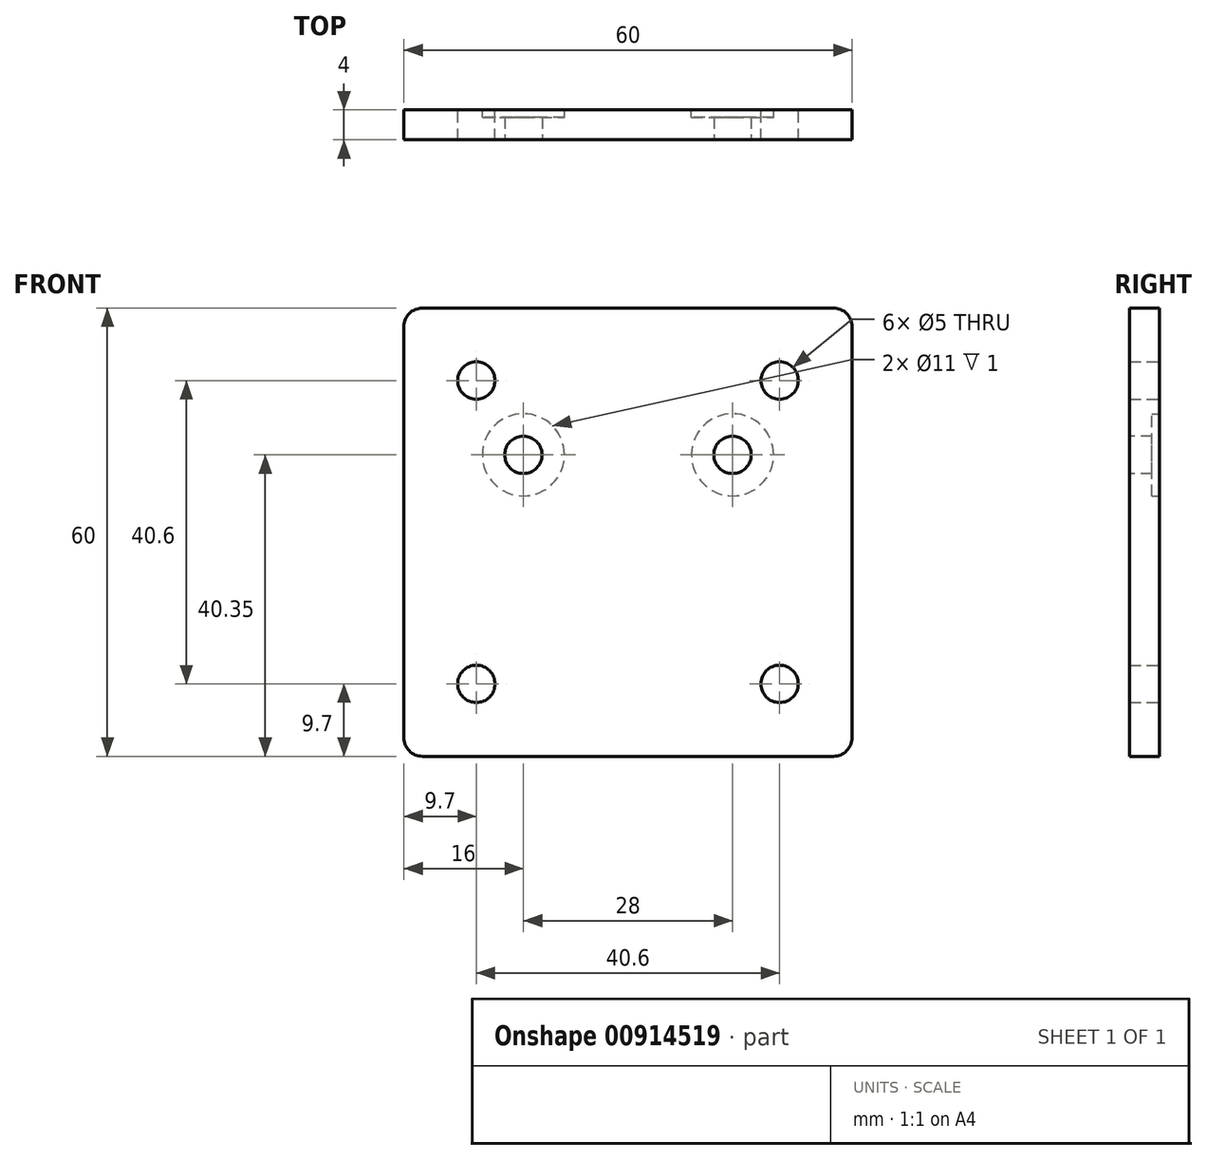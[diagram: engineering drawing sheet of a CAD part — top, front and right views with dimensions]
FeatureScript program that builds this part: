
annotation { "Feature Type Name" : "Feature", "Feature Type Description" : "" }
export const myFeature = defineFeature(function(context is Context, id is Id, definition is map)
    precondition{}
    {
        {
            var Q0;
            Q0=qCreatedBy(makeId("Front.planeOp"),FACE);
            var sketch = newSketch(context, id + "F0", { "sketchPlane" : qUnion([Q0])});
            skLineSegment(sketch, "E0.bottom", {"start": v(30, 30) * mm, "end": v(-30, 30) * mm});
            skLineSegment(sketch, "E0.top", {"start": v(30, -30) * mm, "end": v(-30, -30) * mm});
            skLineSegment(sketch, "E0.left", {"start": v(30, 30) * mm, "end": v(30, -30) * mm});
            skLineSegment(sketch, "E0.right", {"start": v(-30, 30) * mm, "end": v(-30, -30) * mm});
            skPoint(sketch, "E0.middle", {"position": v(0, 0) * mm});
            skLineSegment(sketch, "E1", {"start": v(20.3, 30) * mm, "end": v(20.3, -30) * mm, "construction": true});
            skLineSegment(sketch, "E2", {"start": v(30, 20.3) * mm, "end": v(-30, 20.3) * mm, "construction": true});
            skLineSegment(sketch, "E3.MirrorCS", {"start": v(-20.3, 30) * mm, "end": v(-20.3, -30) * mm, "construction": true});
            skLineSegment(sketch, "E4.MirrorCS", {"start": v(30, -20.3) * mm, "end": v(-30, -20.3) * mm, "construction": true});
            skPoint(sketch, "E5", {"position": v(-20.3, 20.3) * mm});
            skPoint(sketch, "E6", {"position": v(20.3, 20.3) * mm});
            skPoint(sketch, "E7", {"position": v(20.3, -20.3) * mm});
            skPoint(sketch, "E8", {"position": v(-20.3, -20.3) * mm});
            skSolve(sketch);
        }
        {
            var Q0;
            Q0=qSketchRegion(id+"F0",true);
            extrude(context, id + "F1", {"entities" : qUnion([Q0]), "depth" : 4 * mm, "offsetDistance" : 25 * mm});
        }
        {
            var Q0;
            Q0=sQuery(id+"F0.wireOp",VERTEX,"E8");
            var Q1;
            Q1=sQuery(id+"F0.wireOp",VERTEX,"E7");
            var Q2;
            Q2=sQuery(id+"F0.wireOp",VERTEX,"E6");
            var Q3;
            Q3=sQuery(id+"F0.wireOp",VERTEX,"E5");
            var Q4;
            Q4=makeQuery(id+"F1.opExtrude","SWEPT_BODY",BODY,{"disambiguationData":[OSD([sQuery(id+"F0.wireOp",EDGE,"E0.bottom"),sQuery(id+"F0.wireOp",EDGE,"E0.top"),sQuery(id+"F0.wireOp",EDGE,"E0.left"),sQuery(id+"F0.wireOp",EDGE,"E0.right")])]});
            hole(context, id + "F2", {"style" : HoleStyle.SIMPLE, "endStyle" : HoleEndStyle.THROUGH, "oppositeDirection" : true, "holeDiameter" : 5 * mm, "majorDiameter" : 5 * mm, "isTappedThrough" : true, "tappedDepth" : 12 * mm, "tapClearance" : 3, "locations" : qUnion([Q0, Q1, Q2, Q3]), "scope" : qUnion([Q4])});
        }
        {
            var Q0;
            Q0=makeQuery(id+"F1.opExtrude","CAP_FACE",FACE,{"disambiguationData":[OSD([sQuery(id+"F0.wireOp",EDGE,"E0.bottom"),sQuery(id+"F0.wireOp",EDGE,"E0.top"),sQuery(id+"F0.wireOp",EDGE,"E0.left"),sQuery(id+"F0.wireOp",EDGE,"E0.right")])],"isStart":false});
            var sketch = newSketch(context, id + "F3", { "sketchPlane" : qUnion([Q0])});
            skPoint(sketch, "E9", {"position": v(-14, 10.35) * mm});
            skLineSegment(sketch, "E10", {"start": v(-14, 10.35) * mm, "end": v(0, 10.35) * mm, "construction": true});
            skLineSegment(sketch, "E11", {"start": v(14, 10.35) * mm, "end": v(0, 10.35) * mm, "construction": true});
            skPoint(sketch, "E12", {"position": v(14, 10.35) * mm});
            skSolve(sketch);
        }
        {
            var Q0;
            Q0=sQuery(id+"F3.wireOp",VERTEX,"E9");
            var Q1;
            Q1=sQuery(id+"F3.wireOp",VERTEX,"E11.start");
            var Q2;
            Q2=makeQuery(id+"F1.opExtrude","SWEPT_BODY",BODY,{"disambiguationData":[OSD([sQuery(id+"F0.wireOp",EDGE,"E0.bottom"),sQuery(id+"F0.wireOp",EDGE,"E0.top"),sQuery(id+"F0.wireOp",EDGE,"E0.left"),sQuery(id+"F0.wireOp",EDGE,"E0.right")])]});
            hole(context, id + "F4", {"style" : HoleStyle.SIMPLE, "endStyle" : HoleEndStyle.THROUGH, "holeDiameter" : 5 * mm, "majorDiameter" : 5 * mm, "isTappedThrough" : true, "tappedDepth" : 12 * mm, "tapClearance" : 3, "locations" : qUnion([Q0, Q1]), "scope" : qUnion([Q2])});
        }
        {
            var Q0;
            Q0=makeQuery(id+"F0.imprint","IMPRINT",FACE,{"disambiguationData":[TD([[makeQuery(id+"F0.imprint","IMPRINT",EDGE,{"derivedFrom":sQuery(id+"F0.wireOp",EDGE,"E0.bottom")}),1.0]])]});
            var sketch = newSketch(context, id + "F5", { "sketchPlane" : qUnion([Q0])});
            skCircle(sketch, "E13.0", {"center": v(14, 10.35) * mm, "radius": 2.5 * mm, "construction": true});
            skCircle(sketch, "E13.1", {"center": v(-14, 10.35) * mm, "radius": 2.5 * mm, "construction": true});
            skCircle(sketch, "E14", {"center": v(14, 10.35) * mm, "radius": 5.5 * mm});
            skCircle(sketch, "E15", {"center": v(-14, 10.35) * mm, "radius": 5.5 * mm});
            skSolve(sketch);
        }
        {
            var Q0;
            Q0=qSketchRegion(id+"F5",true);
            extrude(context, id + "F6", {"entities" : qUnion([Q0]), "operationType" : NewBodyOperationType.REMOVE, "depth" : 1 * mm, "offsetDistance" : 25 * mm});
        }
        {
            var Q0;
            Q0=makeQuery(id+"F1.opExtrude","SWEPT_EDGE",EDGE,{"disambiguationData":[OSD([sQuery(id+"F0.wireOp",EDGE,"E0.bottom"),sQuery(id+"F0.wireOp",EDGE,"E0.left")])]});
            var Q1;
            Q1=makeQuery(id+"F1.opExtrude","SWEPT_EDGE",EDGE,{"disambiguationData":[OSD([sQuery(id+"F0.wireOp",EDGE,"E0.top"),sQuery(id+"F0.wireOp",EDGE,"E0.left")])]});
            var Q2;
            Q2=makeQuery(id+"F1.opExtrude","SWEPT_EDGE",EDGE,{"disambiguationData":[OSD([sQuery(id+"F0.wireOp",EDGE,"E0.top"),sQuery(id+"F0.wireOp",EDGE,"E0.right")])]});
            var Q3;
            Q3=makeQuery(id+"F1.opExtrude","SWEPT_EDGE",EDGE,{"disambiguationData":[OSD([sQuery(id+"F0.wireOp",EDGE,"E0.bottom"),sQuery(id+"F0.wireOp",EDGE,"E0.right")])]});
            fillet(context, id + "F7", {"entities" : qUnion([Q0, Q1, Q2, Q3]), "radius" : 2.5 * mm, "tangentPropagation" : true, "allowEdgeOverflow" : false});
        }
    });
